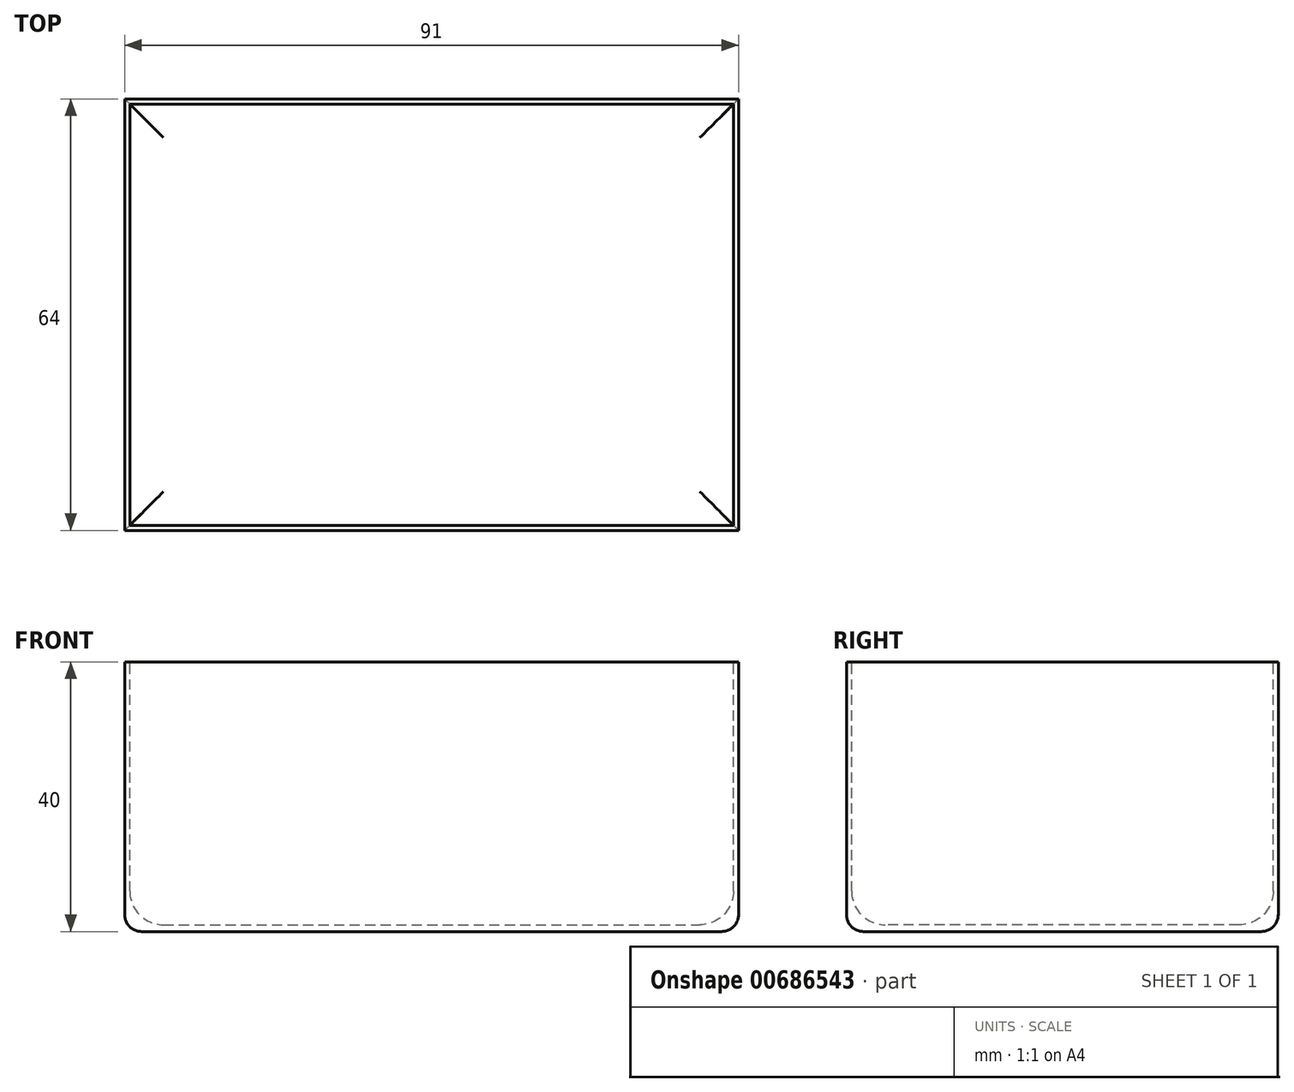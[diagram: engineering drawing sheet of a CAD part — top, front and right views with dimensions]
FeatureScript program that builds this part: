
annotation { "Feature Type Name" : "Feature", "Feature Type Description" : "" }
export const myFeature = defineFeature(function(context is Context, id is Id, definition is map)
    precondition{}
    {
        {
            var Q0;
            Q0=qCreatedBy(makeId("Top.planeOp"),FACE);
            var sketch = newSketch(context, id + "F0", { "sketchPlane" : qUnion([Q0])});
            skLineSegment(sketch, "E0.bottom", {"start": v(45.5, 32) * mm, "end": v(-45.5, 32) * mm});
            skLineSegment(sketch, "E0.top", {"start": v(45.5, -32) * mm, "end": v(-45.5, -32) * mm});
            skLineSegment(sketch, "E0.left", {"start": v(45.5, 32) * mm, "end": v(45.5, -32) * mm});
            skLineSegment(sketch, "E0.right", {"start": v(-45.5, 32) * mm, "end": v(-45.5, -32) * mm});
            skPoint(sketch, "E0.middle", {"position": v(0, 0) * mm});
            skSolve(sketch);
        }
        {
            var Q0;
            Q0=makeQuery(id+"F0.imprint","IMPRINT",FACE,{"disambiguationData":[TD([[makeQuery(id+"F0.imprint","IMPRINT",EDGE,{"derivedFrom":sQuery(id+"F0.wireOp",EDGE,"E0.bottom")}),1.0]])]});
            extrude(context, id + "F1", {"entities" : qUnion([Q0]), "depth" : 40 * mm, "offsetDistance" : 25 * mm});
        }
        {
            var Q0;
            Q0=makeQuery(id+"F1.opExtrude","CAP_FACE",FACE,{"disambiguationData":[OSD([sQuery(id+"F0.wireOp",EDGE,"E0.bottom"),sQuery(id+"F0.wireOp",EDGE,"E0.top"),sQuery(id+"F0.wireOp",EDGE,"E0.left"),sQuery(id+"F0.wireOp",EDGE,"E0.right")])],"isStart":false});
            var sketch = newSketch(context, id + "F2", { "sketchPlane" : qUnion([Q0])});
            skLineSegment(sketch, "E1.bottom", {"start": v(-44.75, 31.25) * mm, "end": v(44.75, 31.25) * mm});
            skLineSegment(sketch, "E1.top", {"start": v(-44.75, -31.25) * mm, "end": v(44.75, -31.25) * mm});
            skLineSegment(sketch, "E1.left", {"start": v(-44.75, 31.25) * mm, "end": v(-44.75, -31.25) * mm});
            skLineSegment(sketch, "E1.right", {"start": v(44.75, 31.25) * mm, "end": v(44.75, -31.25) * mm});
            skPoint(sketch, "E1.middle", {"position": v(0, 0) * mm});
            skSolve(sketch);
        }
        {
            var Q0;
            Q0=makeQuery(id+"F2.imprint","IMPRINT",FACE,{"disambiguationData":[TD([[makeQuery(id+"F2.imprint","IMPRINT",EDGE,{"derivedFrom":sQuery(id+"F2.wireOp",EDGE,"E1.bottom")}),-1.0]])]});
            extrude(context, id + "F3", {"entities" : qUnion([Q0]), "operationType" : NewBodyOperationType.REMOVE, "oppositeDirection" : true, "depth" : 39 * mm, "offsetDistance" : 25 * mm});
        }
        {
            var Q0;
            Q0=makeQuery(id+"F3.boolean.opBoolean","COPY",FACE,{"derivedFrom":makeQuery(id+"F3.opExtrude","CAP_FACE",FACE,{"disambiguationData":[OSD([sQuery(id+"F2.wireOp",EDGE,"E1.bottom"),sQuery(id+"F2.wireOp",EDGE,"E1.top"),sQuery(id+"F2.wireOp",EDGE,"E1.left"),sQuery(id+"F2.wireOp",EDGE,"E1.right")])],"isStart":false})});
            fillet(context, id + "F4", {"entities" : qUnion([Q0]), "radius" : 5 * mm, "tangentPropagation" : true, "allowEdgeOverflow" : false});
        }
        {
            var Q0;
            Q0=makeQuery(id+"F1.opExtrude","CAP_FACE",FACE,{"disambiguationData":[OSD([sQuery(id+"F0.wireOp",EDGE,"E0.bottom"),sQuery(id+"F0.wireOp",EDGE,"E0.top"),sQuery(id+"F0.wireOp",EDGE,"E0.left"),sQuery(id+"F0.wireOp",EDGE,"E0.right")])],"isStart":true});
            fillet(context, id + "F5", {"entities" : qUnion([Q0]), "radius" : 2.5 * mm, "tangentPropagation" : true, "allowEdgeOverflow" : false});
        }
    });
